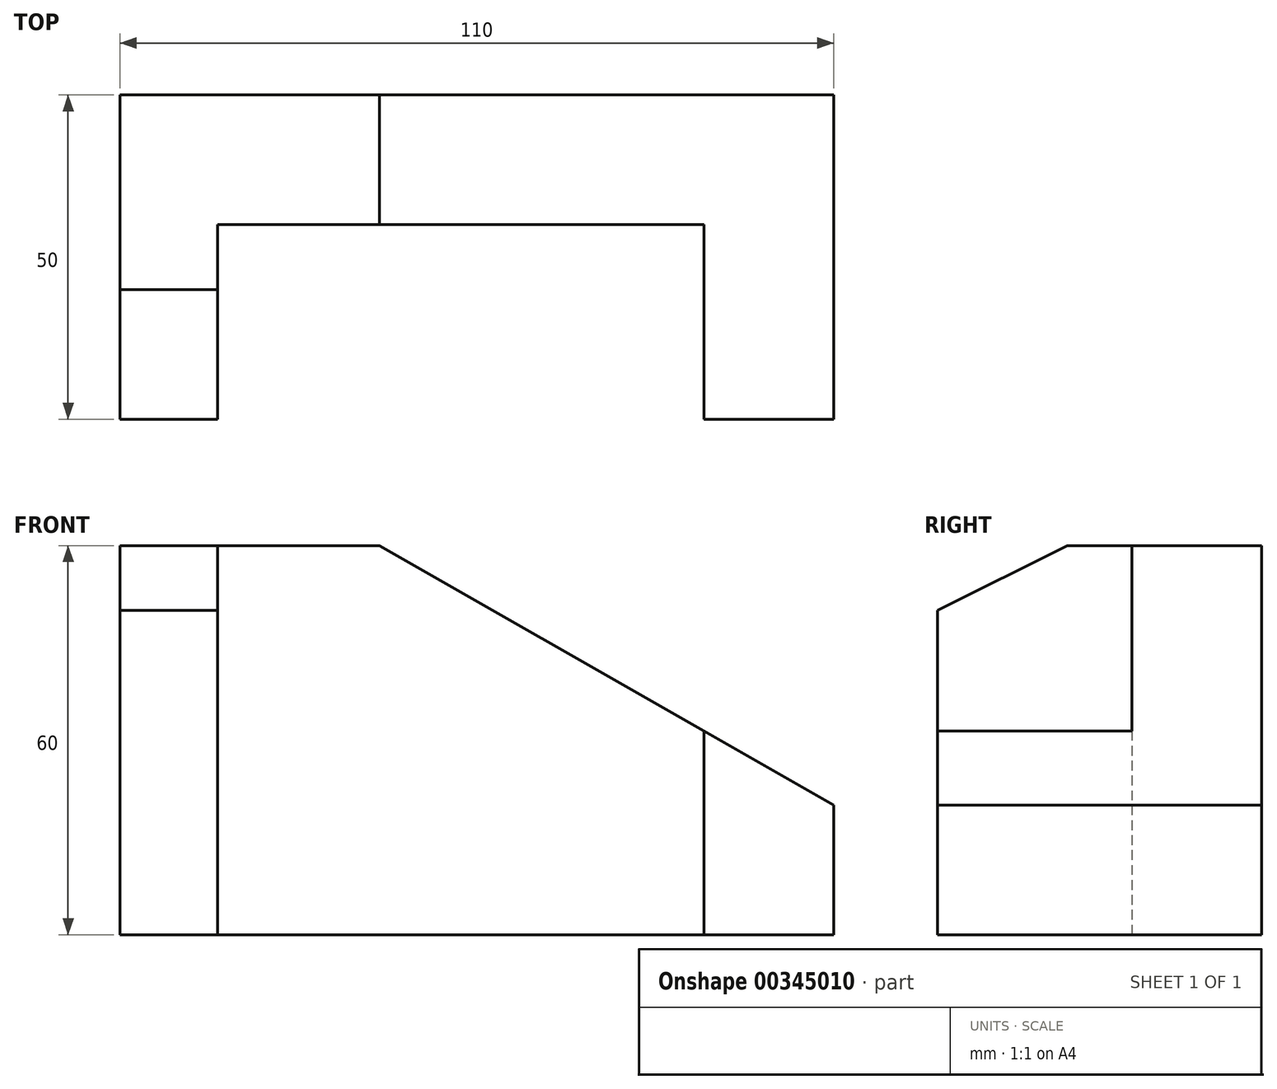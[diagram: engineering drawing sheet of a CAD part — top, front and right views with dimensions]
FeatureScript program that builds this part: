
annotation { "Feature Type Name" : "Feature", "Feature Type Description" : "" }
export const myFeature = defineFeature(function(context is Context, id is Id, definition is map)
    precondition{}
    {
        {
            var Q0;
            Q0=qCreatedBy(makeId("Top.planeOp"),FACE);
            var sketch = newSketch(context, id + "F0", { "sketchPlane" : qUnion([Q0])});
            skLineSegment(sketch, "E0.bottom", {"start": v(55, 25) * mm, "end": v(-55, 25) * mm});
            skLineSegment(sketch, "E0.top", {"start": v(55, -25) * mm, "end": v(35, -25) * mm});
            skLineSegment(sketch, "E0.left", {"start": v(55, 25) * mm, "end": v(55, -25) * mm});
            skLineSegment(sketch, "E0.right", {"start": v(-55, 25) * mm, "end": v(-55, -25) * mm});
            skPoint(sketch, "E0.middle", {"position": v(0, 0) * mm});
            skLineSegment(sketch, "E1.top", {"start": v(-40, 5) * mm, "end": v(35, 5) * mm});
            skLineSegment(sketch, "E1.left", {"start": v(-40, -25) * mm, "end": v(-40, 5) * mm});
            skLineSegment(sketch, "E1.right", {"start": v(35, -25) * mm, "end": v(35, 5) * mm});
            skLineSegment(sketch, "E2.trimOffspring", {"start": v(-40, -25) * mm, "end": v(-55, -25) * mm});
            skSolve(sketch);
        }
        {
            var Q0;
            Q0=makeQuery(id+"F0.imprint","IMPRINT",FACE,{"disambiguationData":[TD([[makeQuery(id+"F0.imprint","IMPRINT",EDGE,{"derivedFrom":sQuery(id+"F0.wireOp",EDGE,"E0.bottom")}),1.0]])]});
            extrude(context, id + "F1", {"entities" : qUnion([Q0]), "depth" : 60 * mm});
        }
        {
            var Q0;
            Q0=makeQuery(id+"F1.opExtrude","SWEPT_FACE",FACE,{"disambiguationData":[OSD([sQuery(id+"F0.wireOp",EDGE,"E0.right")])]});
            var sketch = newSketch(context, id + "F2", { "sketchPlane" : qUnion([Q0])});
            skLineSegment(sketch, "E3.0", {"start": v(5, 60) * mm, "end": v(25, 60) * mm});
            skLineSegment(sketch, "E4.0", {"start": v(-25, 60) * mm, "end": v(-25, 0) * mm});
            skLineSegment(sketch, "E5.0", {"start": v(25, 60) * mm, "end": v(25, 50) * mm});
            skLineSegment(sketch, "E6", {"start": v(5, 60) * mm, "end": v(25, 50) * mm});
            skPoint(sketch, "E7.orphan", {"position": v(25, 0) * mm});
            skSolve(sketch);
        }
        {
            var Q0;
            Q0=makeQuery(id+"F2.imprint","IMPRINT",FACE,{"disambiguationData":[TD([[makeQuery(id+"F2.imprint","IMPRINT",EDGE,{"derivedFrom":sQuery(id+"F2.wireOp",EDGE,"E3.0")}),-1.0]])]});
            extrude(context, id + "F3", {"entities" : qUnion([Q0]), "operationType" : NewBodyOperationType.REMOVE, "oppositeDirection" : true, "depth" : 110 * mm});
        }
        {
            var Q0;
            Q0=makeQuery(id+"F1.opExtrude","SWEPT_FACE",FACE,{"disambiguationData":[OSD([sQuery(id+"F0.wireOp",EDGE,"E0.bottom")])]});
            var sketch = newSketch(context, id + "F4", { "sketchPlane" : qUnion([Q0])});
            skLineSegment(sketch, "E8.0", {"start": v(-55, 60) * mm, "end": v(55, 60) * mm});
            skLineSegment(sketch, "E9.0", {"start": v(-55, 0) * mm, "end": v(55, 0) * mm});
            skLineSegment(sketch, "E10", {"start": v(15, 60) * mm, "end": v(-55, 20) * mm});
            skLineSegment(sketch, "E11", {"start": v(-55, 20) * mm, "end": v(-55, 60) * mm});
            skSolve(sketch);
        }
        {
            var Q0;
            {var subQ2=sQuery(id+"F4.wireOp",EDGE,"E10");Q0=makeQuery(id+"F4.imprint","IMPRINT",FACE,{"disambiguationData":[TD([[makeQuery(id+"F4.imprint","IMPRINT",EDGE,{"derivedFrom":subQ2}),-1.0]])]});}
            extrude(context, id + "F5", {"entities" : qUnion([Q0]), "operationType" : NewBodyOperationType.REMOVE, "oppositeDirection" : true, "depth" : 50 * mm});
        }
    });
